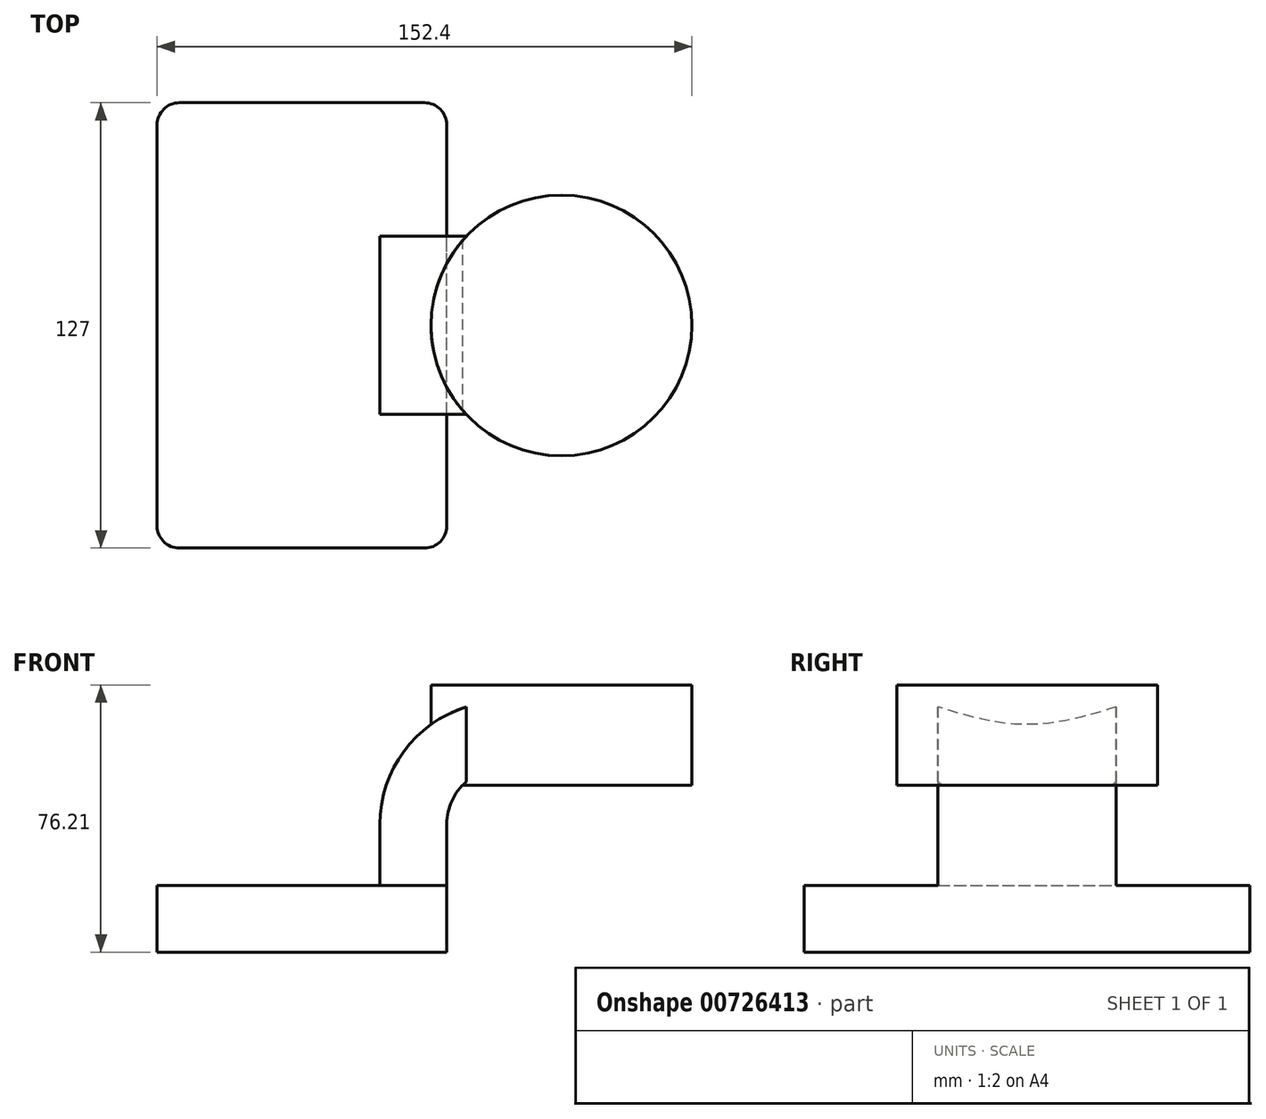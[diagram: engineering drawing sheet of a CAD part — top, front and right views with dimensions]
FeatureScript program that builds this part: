
annotation { "Feature Type Name" : "Feature", "Feature Type Description" : "" }
export const myFeature = defineFeature(function(context is Context, id is Id, definition is map)
    precondition{}
    {
        {
            var Q0;
            Q0=qCreatedBy(makeId("Front.planeOp"),FACE);
            var sketch = newSketch(context, id + "F0", { "sketchPlane" : qUnion([Q0])});
            skLineSegment(sketch, "E0.bottom", {"start": v(-41.28, -9.53) * mm, "end": v(41.28, -9.53) * mm});
            skLineSegment(sketch, "E0.top", {"start": v(-41.28, 9.53) * mm, "end": v(41.28, 9.53) * mm});
            skLineSegment(sketch, "E0.left", {"start": v(-41.28, -9.53) * mm, "end": v(-41.28, 9.53) * mm});
            skLineSegment(sketch, "E0.right", {"start": v(41.28, -9.53) * mm, "end": v(41.28, 9.53) * mm});
            skPoint(sketch, "E0.middle", {"position": v(0, 0) * mm});
            skLineSegment(sketch, "E1.bottom", {"start": v(60.32, 38.1) * mm, "end": v(111.12, 38.1) * mm});
            skLineSegment(sketch, "E1.top", {"start": v(60.32, 66.67) * mm, "end": v(111.12, 66.67) * mm});
            skLineSegment(sketch, "E1.left", {"start": v(60.32, 38.1) * mm, "end": v(60.32, 66.67) * mm});
            skLineSegment(sketch, "E1.right", {"start": v(111.12, 38.1) * mm, "end": v(111.12, 66.67) * mm});
            skPoint(sketch, "E1.middle", {"position": v(85.72, 52.39) * mm});
            skLineSegment(sketch, "E2", {"start": v(41.28, 9.53) * mm, "end": v(41.28, 27) * mm});
            skArc(sketch, "E3", {"start": v(41.28, 27) * mm, "mid": v(45.92, 38.23) * mm, "end": v(57.15, 42.88) * mm});
            skLineSegment(sketch, "E4", {"start": v(57.15, 42.88) * mm, "end": v(73.39, 42.88) * mm});
            skLineSegment(sketch, "E5.0", {"start": v(57.15, 61.93) * mm, "end": v(73.39, 61.93) * mm});
            skArc(sketch, "E5.1", {"start": v(22.23, 27) * mm, "mid": v(32.45, 51.7) * mm, "end": v(57.15, 61.93) * mm});
            skLineSegment(sketch, "E5.2", {"start": v(22.23, 9.53) * mm, "end": v(22.23, 27) * mm});
            skLineSegment(sketch, "E6", {"start": v(73.96, 66.67) * mm, "end": v(73.96, 38.1) * mm});
            skFitSpline(sketch, "E7", {"points": [v(-41.28, 9.53) * mm, v(57.15, 61.93) * mm], "startDerivative": vector(33.05, 74.78) * mm, "endDerivative": vector(111.35, -3.92) * mm});
            skSolve(sketch);
        }
        {
            var Q0;
            Q0=makeQuery(id+"F0.imprint","IMPRINT",FACE,{"disambiguationData":[TD([[makeQuery(id+"F0.imprint","IMPRINT",EDGE,{"derivedFrom":sQuery(id+"F0.wireOp",EDGE,"E0.bottom")}),1.0]])]});
            extrude(context, id + "F1", {"entities" : qUnion([Q0]), "endBound" : BoundingType.SYMMETRIC, "depth" : 127 * mm, "offsetDistance" : 25.4 * mm});
        }
        {
            var Q0;
            {var subQ1=sQuery(id+"F0.wireOp",EDGE,"E2");Q0=makeQuery(id+"F0.imprint","IMPRINT",FACE,{"disambiguationData":[TD([[makeQuery(id+"F0.imprint","IMPRINT",EDGE,{"derivedFrom":subQ1}),1.0]])]});}
            var Q1;
            {var subQ6=sQuery(id+"F0.wireOp",EDGE,"E6");Q1=makeQuery(id+"F0.imprint","IMPRINT",FACE,{"disambiguationData":[TD([[makeQuery(id+"F0.imprint","IMPRINT",EDGE,{"derivedFrom":subQ6}),-1.0]])]});}
            extrude(context, id + "F2", {"entities" : qUnion([Q0, Q1]), "operationType" : NewBodyOperationType.ADD, "endBound" : BoundingType.SYMMETRIC, "depth" : 50.8 * mm, "offsetDistance" : 25.4 * mm});
        }
        {
            var Q0;
            Q0=makeQuery(id+"F0.imprint","IMPRINT",FACE,{"disambiguationData":[TD([[makeQuery(id+"F0.imprint","IMPRINT",EDGE,{"derivedFrom":sQuery(id+"F0.wireOp",EDGE,"E5.1")}),1.0]])]});
            extrude(context, id + "F3", {"entities" : qUnion([Q0]), "operationType" : NewBodyOperationType.ADD, "endBound" : BoundingType.SYMMETRIC, "depth" : 15.88 * mm, "offsetDistance" : 25.4 * mm});
        }
        {
            var Q0;
            {var subQ0=sQuery(id+"F0.wireOp",EDGE,"E1.right");Q0=makeQuery(id+"F0.imprint","IMPRINT",FACE,{"disambiguationData":[TD([[makeQuery(id+"F0.imprint","IMPRINT",EDGE,{"derivedFrom":subQ0}),1.0]])]});}
            var Q1;
            Q1=sQuery(id+"F0.wireOp",EDGE,"E6");
            revolve(context, id + "F4", {"operationType" : NewBodyOperationType.ADD, "surfaceOperationType" : NewSurfaceOperationType.NEW, "entities" : qUnion([Q0]), "axis" : qUnion([Q1]), "revolveType" : RevolveType.FULL});
        }
        {
            var Q0;
            Q0=makeQuery(id+"F1.opExtrude","CAP_EDGE",EDGE,{"disambiguationData":[OSD([sQuery(id+"F0.wireOp",EDGE,"E0.left")])],"isStart":false});
            var Q1;
            Q1=makeQuery(id+"F1.opExtrude","CAP_EDGE",EDGE,{"disambiguationData":[OSD([sQuery(id+"F0.wireOp",EDGE,"E0.right")])],"isStart":false});
            var Q2;
            Q2=makeQuery(id+"F1.opExtrude","CAP_EDGE",EDGE,{"disambiguationData":[OSD([sQuery(id+"F0.wireOp",EDGE,"E0.left")])],"isStart":true});
            var Q3;
            Q3=makeQuery(id+"F1.opExtrude","CAP_EDGE",EDGE,{"disambiguationData":[OSD([sQuery(id+"F0.wireOp",EDGE,"E0.right")])],"isStart":true});
            fillet(context, id + "F5", {"entities" : qUnion([Q0, Q1, Q2, Q3]), "radius" : 6.35 * mm, "tangentPropagation" : true, "allowEdgeOverflow" : false});
        }
    });
